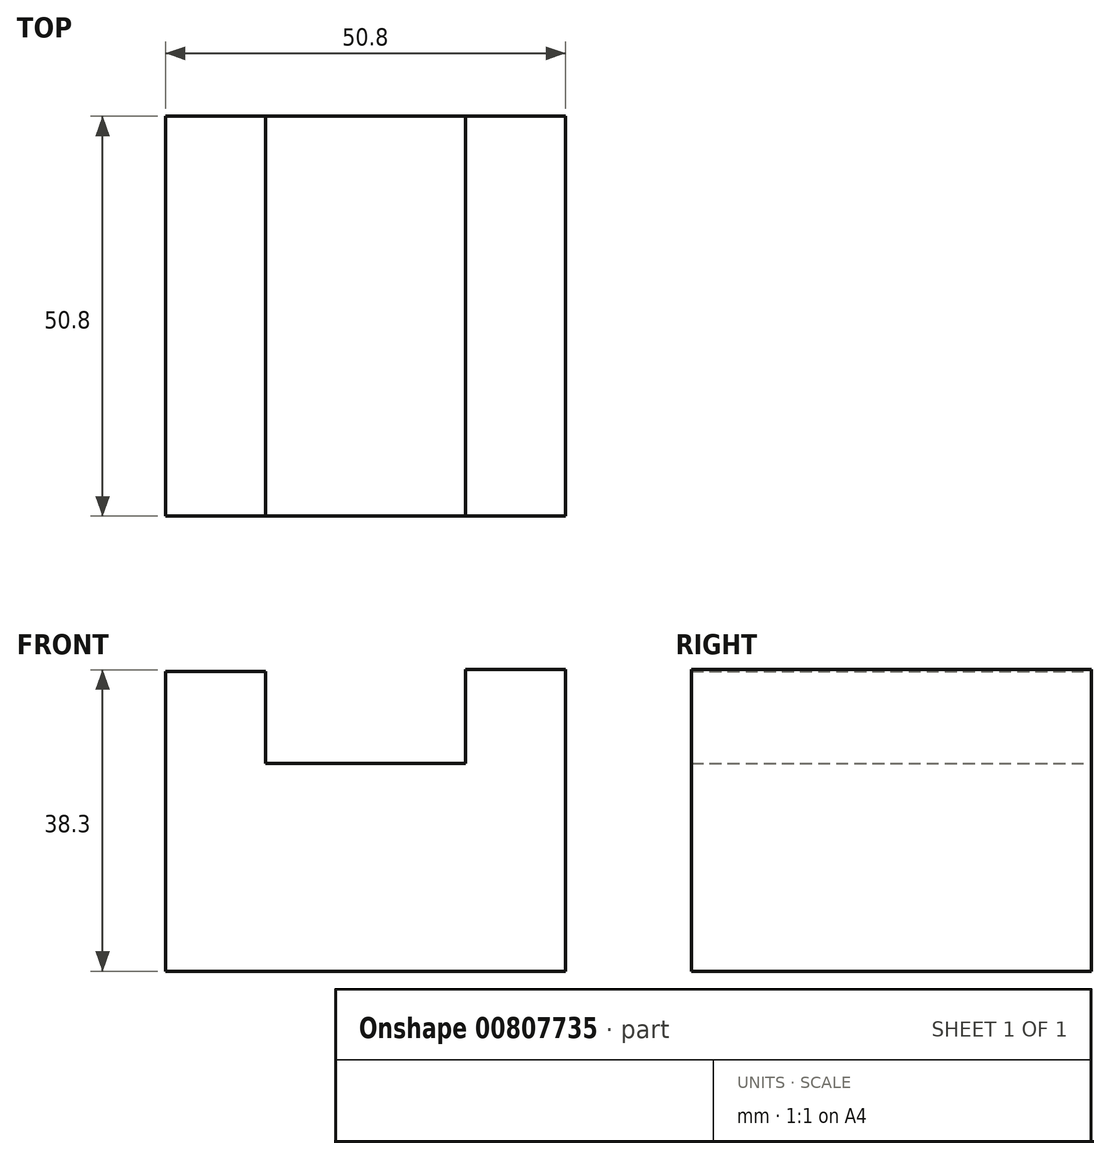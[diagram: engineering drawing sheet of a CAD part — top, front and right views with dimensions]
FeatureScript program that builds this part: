
annotation { "Feature Type Name" : "Feature", "Feature Type Description" : "" }
export const myFeature = defineFeature(function(context is Context, id is Id, definition is map)
    precondition{}
    {
        {
            var Q0;
            Q0=qCreatedBy(makeId("Front.planeOp"),FACE);
            var sketch = newSketch(context, id + "F0", { "sketchPlane" : qUnion([Q0])});
            skLineSegment(sketch, "E0", {"start": v(0, 0) * mm, "end": v(0, 38.1) * mm});
            skLineSegment(sketch, "E1", {"start": v(0, 38.1) * mm, "end": v(12.7, 38.1) * mm});
            skLineSegment(sketch, "E2", {"start": v(12.7, 38.1) * mm, "end": v(12.7, 26.39) * mm});
            skLineSegment(sketch, "E3", {"start": v(12.7, 26.39) * mm, "end": v(38.1, 26.39) * mm});
            skLineSegment(sketch, "E4", {"start": v(38.1, 26.39) * mm, "end": v(38.1, 38.3) * mm});
            skLineSegment(sketch, "E5", {"start": v(38.1, 38.3) * mm, "end": v(50.8, 38.3) * mm});
            skLineSegment(sketch, "E6", {"start": v(50.8, 38.3) * mm, "end": v(50.8, 0) * mm});
            skLineSegment(sketch, "E7", {"start": v(0, 0) * mm, "end": v(50.8, 0) * mm});
            skSolve(sketch);
        }
        {
            var Q0;
            Q0 = qSketchRegion(id + "F0", true);
            extrude(context, id + "F1", {"entities" : qUnion([Q0]), "depth" : 25.4 * mm, "offsetDistance" : 25.4 * mm, "hasSecondDirection" : true, "secondDirectionOppositeDirection" : true, "secondDirectionDepth" : 25.4 * mm});
        }
    });
